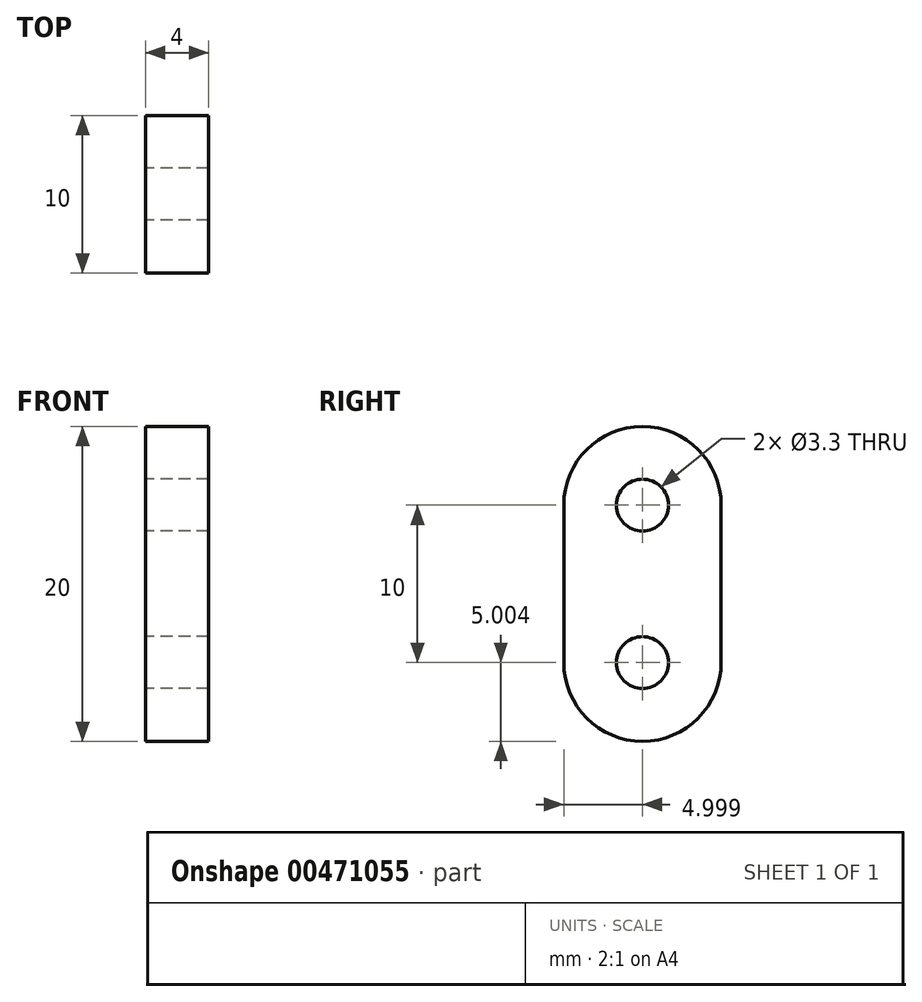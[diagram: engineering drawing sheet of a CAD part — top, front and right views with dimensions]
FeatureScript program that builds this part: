
annotation { "Feature Type Name" : "Feature", "Feature Type Description" : "" }
export const myFeature = defineFeature(function(context is Context, id is Id, definition is map)
    precondition{}
    {
        {
            var Q0;
            Q0=qCreatedBy(makeId("Right.planeOp"),FACE);
            var sketch = newSketch(context, id + "F0", { "sketchPlane" : qUnion([Q0])});
            skLineSegment(sketch, "E0", {"start": v(-58.82, -4.13) * mm, "end": v(-58.82, -14.13) * mm});
            skLineSegment(sketch, "E1", {"start": v(-48.82, -4.13) * mm, "end": v(-48.82, -14.13) * mm});
            skArc(sketch, "E2", {"start": v(-48.82, -4.13) * mm, "mid": v(-53.82, 0.87) * mm, "end": v(-58.82, -4.13) * mm});
            skArc(sketch, "E3", {"start": v(-58.82, -14.13) * mm, "mid": v(-53.82, -19.13) * mm, "end": v(-48.82, -14.13) * mm});
            skCircle(sketch, "E4", {"center": v(-53.82, -4.13) * mm, "radius": 1.65 * mm});
            skCircle(sketch, "E5", {"center": v(-53.82, -14.13) * mm, "radius": 1.65 * mm});
            skSolve(sketch);
        }
        {
            var Q0;
            Q0 = qSketchRegion(id + "F0", true);
            extrude(context, id + "F1", {"entities" : qUnion([Q0]), "depth" : 4 * mm, "offsetDistance" : 25 * mm});
        }
    });
